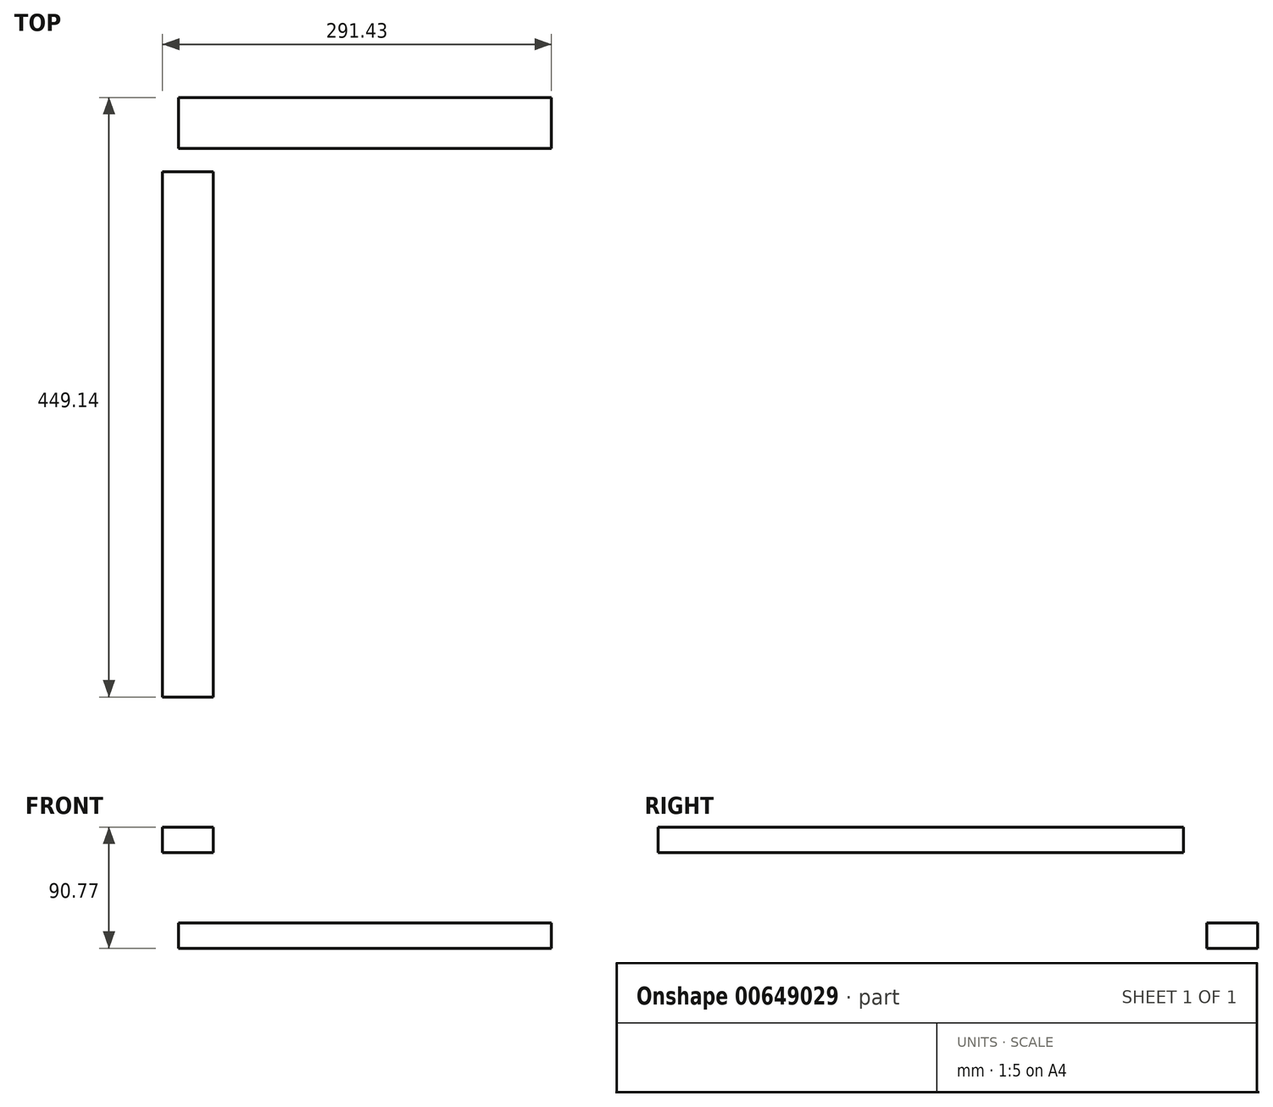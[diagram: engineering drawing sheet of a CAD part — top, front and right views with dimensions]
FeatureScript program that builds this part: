
annotation { "Feature Type Name" : "Feature", "Feature Type Description" : "" }
export const myFeature = defineFeature(function(context is Context, id is Id, definition is map)
    precondition{}
    {
        {
            var Q0;
            Q0=qCreatedBy(makeId("Right.planeOp"),FACE);
            var sketch = newSketch(context, id + "F0", { "sketchPlane" : qUnion([Q0])});
            skLineSegment(sketch, "E0.bottom", {"start": v(17.34, -37.58) * mm, "end": v(55.44, -37.58) * mm});
            skLineSegment(sketch, "E0.top", {"start": v(17.34, -56.63) * mm, "end": v(55.44, -56.63) * mm});
            skLineSegment(sketch, "E0.left", {"start": v(17.34, -37.58) * mm, "end": v(17.34, -56.63) * mm});
            skLineSegment(sketch, "E0.right", {"start": v(55.44, -37.58) * mm, "end": v(55.44, -56.63) * mm});
            skSolve(sketch);
        }
        {
            var Q0;
            Q0=makeQuery(id+"F0.imprint","IMPRINT",FACE,{"disambiguationData":[TD([[makeQuery(id+"F0.imprint","IMPRINT",EDGE,{"derivedFrom":sQuery(id+"F0.wireOp",EDGE,"E0.bottom")}),-1.0]])]});
            extrude(context, id + "F1", {"entities" : qUnion([Q0]), "flatOperationType" : FlatOperationType.REMOVE, "depth" : 279.4 * mm, "offsetDistance" : 25.4 * mm, "domain" : OperationDomain.MODEL});
        }
        {
            var Q0;
            Q0=qCreatedBy(makeId("Front.planeOp"),FACE);
            var sketch = newSketch(context, id + "F2", { "sketchPlane" : qUnion([Q0])});
            skLineSegment(sketch, "E1.bottom", {"start": v(26.07, 34.14) * mm, "end": v(-12.03, 34.14) * mm});
            skLineSegment(sketch, "E1.top", {"start": v(26.07, 15.1) * mm, "end": v(-12.03, 15.1) * mm});
            skLineSegment(sketch, "E1.left", {"start": v(26.07, 34.14) * mm, "end": v(26.07, 15.1) * mm});
            skLineSegment(sketch, "E1.right", {"start": v(-12.03, 34.14) * mm, "end": v(-12.03, 15.1) * mm});
            skSolve(sketch);
        }
        {
            var Q0;
            Q0=makeQuery(id+"F2.imprint","IMPRINT",FACE,{"disambiguationData":[TD([[makeQuery(id+"F2.imprint","IMPRINT",EDGE,{"derivedFrom":sQuery(id+"F2.wireOp",EDGE,"E1.bottom")}),1.0]])]});
            extrude(context, id + "F3", {"entities" : qUnion([Q0]), "flatOperationType" : FlatOperationType.REMOVE, "depth" : 393.7 * mm, "offsetDistance" : 25.4 * mm, "domain" : OperationDomain.MODEL});
        }
    });
